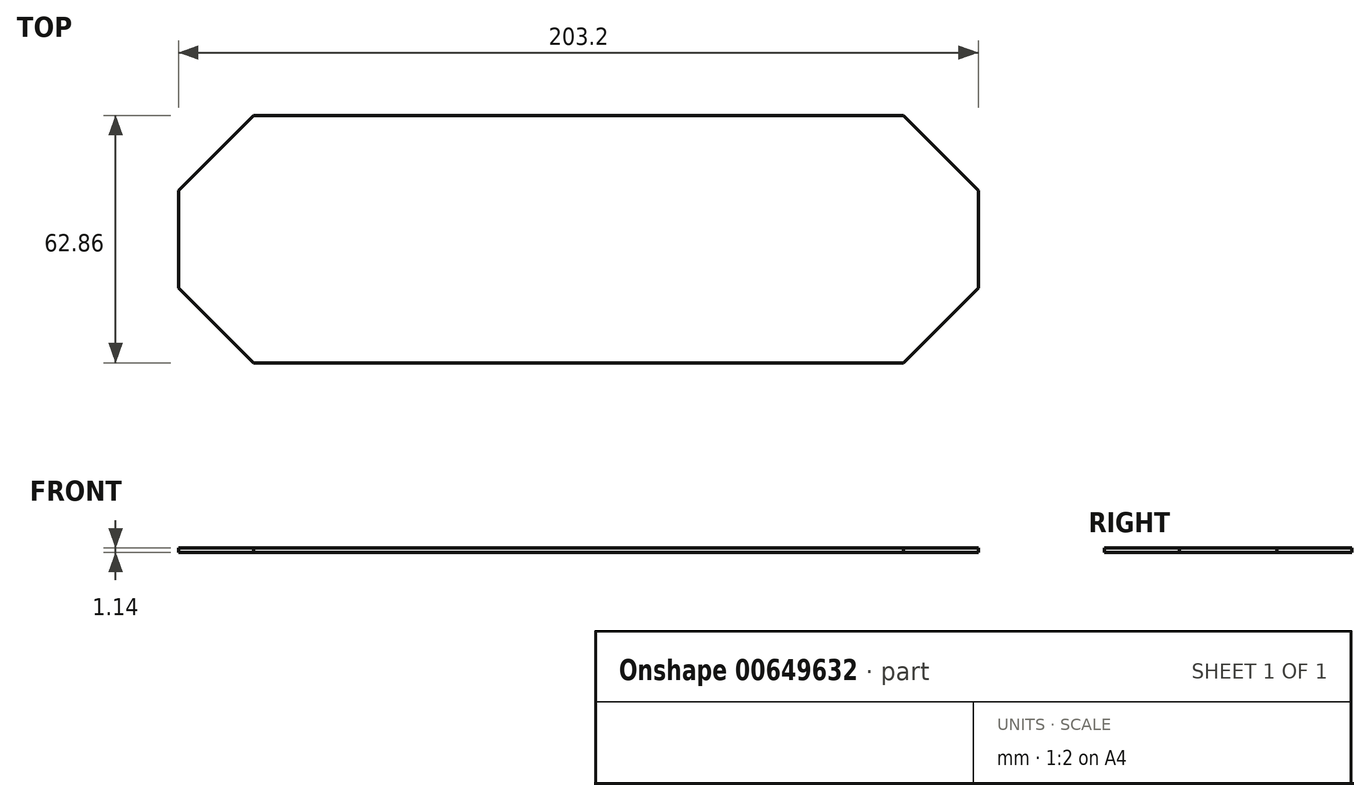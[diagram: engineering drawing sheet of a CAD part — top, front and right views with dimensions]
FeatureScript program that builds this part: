
annotation { "Feature Type Name" : "Feature", "Feature Type Description" : "" }
export const myFeature = defineFeature(function(context is Context, id is Id, definition is map)
    precondition{}
    {
        {
            var Q0;
            Q0=qCreatedBy(makeId("Top.planeOp"),FACE);
            var sketch = newSketch(context, id + "F0", { "sketchPlane" : qUnion([Q0])});
            skLineSegment(sketch, "E0.bottom", {"start": v(101.6, -31.43) * mm, "end": v(-101.6, -31.43) * mm});
            skLineSegment(sketch, "E0.top", {"start": v(101.6, 31.43) * mm, "end": v(-101.6, 31.43) * mm});
            skLineSegment(sketch, "E0.left", {"start": v(101.6, -31.43) * mm, "end": v(101.6, 31.43) * mm});
            skLineSegment(sketch, "E0.right", {"start": v(-101.6, -31.43) * mm, "end": v(-101.6, 31.43) * mm});
            skPoint(sketch, "E0.middle", {"position": v(0, 0) * mm});
            skSolve(sketch);
        }
        {
            var Q0;
            Q0=makeQuery(id+"F0.imprint","IMPRINT",FACE,{"disambiguationData":[TD([[makeQuery(id+"F0.imprint","IMPRINT",EDGE,{"derivedFrom":sQuery(id+"F0.wireOp",EDGE,"E0.bottom")}),-1.0]])]});
            extrude(context, id + "F1", {"entities" : qUnion([Q0]), "depth" : 1.14 * mm, "offsetDistance" : 25.4 * mm});
        }
        {
            var Q0;
            Q0=makeQuery(id+"F1.opExtrude","SWEPT_EDGE",EDGE,{"disambiguationData":[OSD([sQuery(id+"F0.wireOp",EDGE,"E0.bottom"),sQuery(id+"F0.wireOp",EDGE,"E0.right")])]});
            var Q1;
            Q1=makeQuery(id+"F1.opExtrude","SWEPT_EDGE",EDGE,{"disambiguationData":[OSD([sQuery(id+"F0.wireOp",EDGE,"E0.top"),sQuery(id+"F0.wireOp",EDGE,"E0.right")])]});
            var Q2;
            Q2=makeQuery(id+"F1.opExtrude","SWEPT_EDGE",EDGE,{"disambiguationData":[OSD([sQuery(id+"F0.wireOp",EDGE,"E0.top"),sQuery(id+"F0.wireOp",EDGE,"E0.left")])]});
            var Q3;
            Q3=makeQuery(id+"F1.opExtrude","SWEPT_EDGE",EDGE,{"disambiguationData":[OSD([sQuery(id+"F0.wireOp",EDGE,"E0.bottom"),sQuery(id+"F0.wireOp",EDGE,"E0.left")])]});
            chamfer(context, id + "F2", {"entities" : qUnion([Q0, Q1, Q2, Q3]), "width" : 19.05 * mm, "tangentPropagation" : true});
        }
    });
